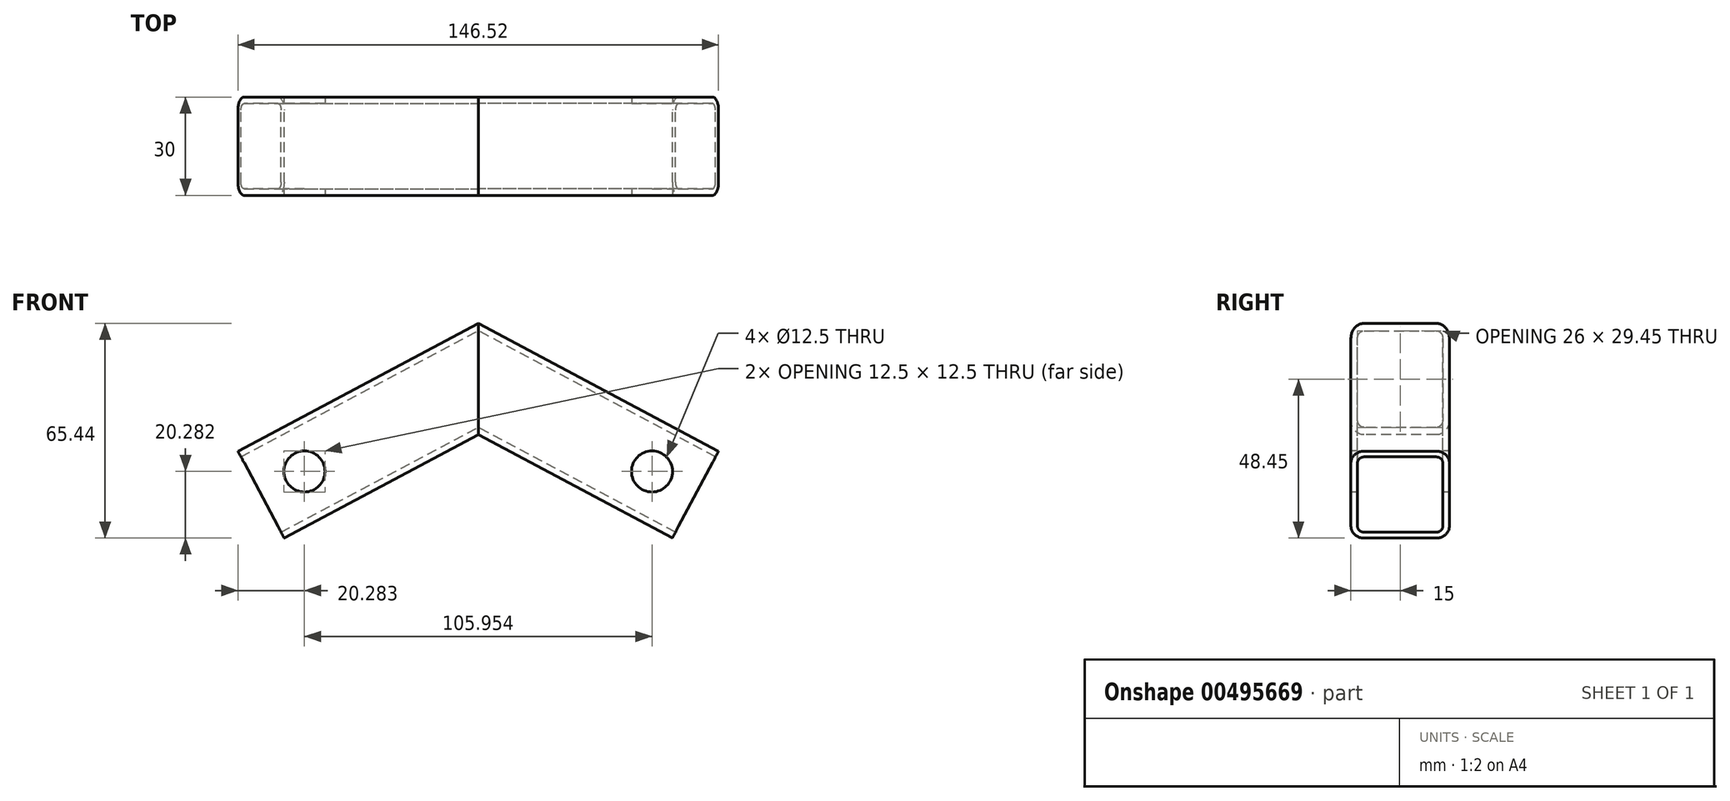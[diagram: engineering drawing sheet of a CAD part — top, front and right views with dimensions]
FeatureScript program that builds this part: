
annotation { "Feature Type Name" : "Feature", "Feature Type Description" : "" }
export const myFeature = defineFeature(function(context is Context, id is Id, definition is map)
    precondition{}
    {
        {
            var Q0;
            Q0=qCreatedBy(makeId("Front.planeOp"),FACE);
            var sketch = newSketch(context, id + "F0", { "sketchPlane" : qUnion([Q0])});
            skLineSegment(sketch, "E0", {"start": v(0, 0) * mm, "end": v(-66.22, -35.21) * mm});
            skSolve(sketch);
        }
        {
            var Q0;
            Q0=sQuery(id+"F0.wireOp",VERTEX,"E0.end");
            var Q1;
            Q1=sQuery(id+"F0.wireOp",EDGE,"E0");
            cPlane(context, id + "F1", {"entities" : qUnion([Q0, Q1]), "cplaneType" : CPlaneType.LINE_POINT, "offset" : 25 * mm, "width" : 150 * mm, "height" : 150 * mm});
        }
        {
            var Q0;
            Q0=qCreatedBy(id+"F1.planeOp",FACE);
            var sketch = newSketch(context, id + "F2", { "sketchPlane" : qUnion([Q0])});
            skLineSegment(sketch, "E1.bottom", {"start": v(11, -15) * mm, "end": v(-11, -15) * mm});
            skLineSegment(sketch, "E1.top", {"start": v(11, 15) * mm, "end": v(-11, 15) * mm});
            skLineSegment(sketch, "E1.left", {"start": v(15, -11) * mm, "end": v(15, 11) * mm});
            skLineSegment(sketch, "E1.right", {"start": v(-15, -11) * mm, "end": v(-15, 11) * mm});
            skPoint(sketch, "E1.middle", {"position": v(0, 0) * mm});
            skPoint(sketch, "E2.visualSharp", {"position": v(-15, 15) * mm});
            skArc(sketch, "E2.filletArc", {"start": v(-11, 15) * mm, "mid": v(-13.83, 13.83) * mm, "end": v(-15, 11) * mm});
            skPoint(sketch, "E3.visualSharp", {"position": v(-15, -15) * mm});
            skArc(sketch, "E3.filletArc", {"start": v(-15, -11) * mm, "mid": v(-13.83, -13.83) * mm, "end": v(-11, -15) * mm});
            skPoint(sketch, "E4.visualSharp", {"position": v(15, -15) * mm});
            skArc(sketch, "E4.filletArc", {"start": v(11, -15) * mm, "mid": v(13.83, -13.83) * mm, "end": v(15, -11) * mm});
            skPoint(sketch, "E5.visualSharp", {"position": v(15, 15) * mm});
            skArc(sketch, "E5.filletArc", {"start": v(15, 11) * mm, "mid": v(13.83, 13.83) * mm, "end": v(11, 15) * mm});
            skArc(sketch, "E6.0", {"start": v(-13, -11) * mm, "mid": v(-12.41, -12.41) * mm, "end": v(-11, -13) * mm});
            skLineSegment(sketch, "E6.1", {"start": v(11, -13) * mm, "end": v(-11, -13) * mm});
            skLineSegment(sketch, "E6.2", {"start": v(-13, -11) * mm, "end": v(-13, 11) * mm});
            skArc(sketch, "E6.3", {"start": v(11, -13) * mm, "mid": v(12.41, -12.41) * mm, "end": v(13, -11) * mm});
            skArc(sketch, "E6.4", {"start": v(-11, 13) * mm, "mid": v(-12.41, 12.41) * mm, "end": v(-13, 11) * mm});
            skLineSegment(sketch, "E6.5", {"start": v(11, 13) * mm, "end": v(-11, 13) * mm});
            skArc(sketch, "E6.6", {"start": v(13, 11) * mm, "mid": v(12.41, 12.41) * mm, "end": v(11, 13) * mm});
            skLineSegment(sketch, "E6.7", {"start": v(13, -11) * mm, "end": v(13, 11) * mm});
            skSolve(sketch);
        }
        {
            var Q0;
            Q0=makeQuery(id+"F2.imprint","IMPRINT",FACE,{"disambiguationData":[TD([[makeQuery(id+"F2.imprint","IMPRINT",EDGE,{"derivedFrom":sQuery(id+"F2.wireOp",EDGE,"E1.bottom")}),-1.0]])]});
            var Q1;
            Q1=sQuery(id+"F0.wireOp",EDGE,"E0");
            sweep(context, id + "F3", {"profiles" : qUnion([Q0]), "path" : qUnion([Q1])});
        }
        {
            var Q0;
            Q0=makeQuery(id+"F3.opSweep","CAP_FACE",FACE,{"disambiguationData":[OSD([sQuery(id+"F0.wireOp",VERTEX,"E0.start"),sQuery(id+"F2.wireOp",EDGE,"E1.bottom"),sQuery(id+"F2.wireOp",EDGE,"E1.top"),sQuery(id+"F2.wireOp",EDGE,"E1.left"),sQuery(id+"F2.wireOp",EDGE,"E1.right"),sQuery(id+"F2.wireOp",EDGE,"E2.filletArc"),sQuery(id+"F2.wireOp",EDGE,"E3.filletArc"),sQuery(id+"F2.wireOp",EDGE,"E4.filletArc"),sQuery(id+"F2.wireOp",EDGE,"E5.filletArc"),sQuery(id+"F2.wireOp",EDGE,"E6.0"),sQuery(id+"F2.wireOp",EDGE,"E6.1"),sQuery(id+"F2.wireOp",EDGE,"E6.2"),sQuery(id+"F2.wireOp",EDGE,"E6.3"),sQuery(id+"F2.wireOp",EDGE,"E6.4"),sQuery(id+"F2.wireOp",EDGE,"E6.5"),sQuery(id+"F2.wireOp",EDGE,"E6.6"),sQuery(id+"F2.wireOp",EDGE,"E6.7")])],"isStart":false});
            extrude(context, id + "F4", {"entities" : qUnion([Q0]), "operationType" : NewBodyOperationType.ADD, "depth" : 25 * mm});
        }
        {
            var Q0;
            {var subQ0=sQuery(id+"F2.wireOp",EDGE,"E1.left");Q0=makeQuery(id+"F4.boolean.opBoolean","MERGE",FACE,{"derivedFrom":[makeQuery(id+"F3.opSweep","SWEPT_FACE",FACE,{"disambiguationData":[OSD([sQuery(id+"F0.wireOp",EDGE,"E0"),subQ0])]}),makeQuery(id+"F4.opExtrude","SWEPT_FACE",FACE,{"disambiguationData":[OSD([sQuery(id+"F0.wireOp",VERTEX,"E0.start"),subQ0])]})]});}
            var sketch = newSketch(context, id + "F5", { "sketchPlane" : qUnion([Q0])});
            skLineSegment(sketch, "E7", {"start": v(0, 16.99) * mm, "end": v(0, -16.99) * mm});
            skLineSegment(sketch, "E8", {"start": v(0, -16.99) * mm, "end": v(29.12, -1.5) * mm});
            skLineSegment(sketch, "E9", {"start": v(29.12, -1.5) * mm, "end": v(15.03, 24.98) * mm});
            skLineSegment(sketch, "E10", {"start": v(15.03, 24.98) * mm, "end": v(0, 16.99) * mm});
            skSolve(sketch);
        }
        {
            var Q0;
            Q0 = qSketchRegion(id + "F5", true);
            extrude(context, id + "F6", {"entities" : qUnion([Q0]), "operationType" : NewBodyOperationType.REMOVE, "endBound" : BoundingType.THROUGH_ALL, "oppositeDirection" : true, "depth" : 25 * mm});
        }
        {
            var Q0;
            {var subQ0=sQuery(id+"F2.wireOp",EDGE,"E1.left");Q0=makeQuery(id+"F4.boolean.opBoolean","MERGE",FACE,{"derivedFrom":[makeQuery(id+"F3.opSweep","SWEPT_FACE",FACE,{"disambiguationData":[OSD([sQuery(id+"F0.wireOp",EDGE,"E0"),subQ0])]}),makeQuery(id+"F4.opExtrude","SWEPT_FACE",FACE,{"disambiguationData":[OSD([sQuery(id+"F0.wireOp",VERTEX,"E0.start"),subQ0])]})]});}
            var sketch = newSketch(context, id + "F7", { "sketchPlane" : qUnion([Q0])});
            skLineSegment(sketch, "E11", {"start": v(-66.22, -35.21) * mm, "end": v(-52.98, -28.17) * mm, "construction": true});
            skCircle(sketch, "E12", {"center": v(-52.98, -28.17) * mm, "radius": 6.25 * mm});
            skSolve(sketch);
        }
        {
            var Q0;
            Q0 = qSketchRegion(id + "F7", true);
            extrude(context, id + "F8", {"entities" : qUnion([Q0]), "operationType" : NewBodyOperationType.REMOVE, "endBound" : BoundingType.THROUGH_ALL, "oppositeDirection" : true, "depth" : 25 * mm});
        }
        {
            var Q0;
            Q0=makeQuery(id+"F3.opSweep","SWEPT_BODY",BODY,{"disambiguationData":[OSD([sQuery(id+"F0.wireOp",EDGE,"E0"),sQuery(id+"F2.wireOp",EDGE,"E1.bottom"),sQuery(id+"F2.wireOp",EDGE,"E1.top"),sQuery(id+"F2.wireOp",EDGE,"E1.left"),sQuery(id+"F2.wireOp",EDGE,"E1.right"),sQuery(id+"F2.wireOp",EDGE,"E2.filletArc"),sQuery(id+"F2.wireOp",EDGE,"E3.filletArc"),sQuery(id+"F2.wireOp",EDGE,"E4.filletArc"),sQuery(id+"F2.wireOp",EDGE,"E5.filletArc"),sQuery(id+"F2.wireOp",EDGE,"E6.0"),sQuery(id+"F2.wireOp",EDGE,"E6.1"),sQuery(id+"F2.wireOp",EDGE,"E6.2"),sQuery(id+"F2.wireOp",EDGE,"E6.3"),sQuery(id+"F2.wireOp",EDGE,"E6.4"),sQuery(id+"F2.wireOp",EDGE,"E6.5"),sQuery(id+"F2.wireOp",EDGE,"E6.6"),sQuery(id+"F2.wireOp",EDGE,"E6.7")])]});
            var Q1;
            Q1=makeQuery(id+"F6.boolean.opBoolean","COPY",FACE,{"derivedFrom":makeQuery(id+"F6.opExtrude","SWEPT_FACE",FACE,{"disambiguationData":[OSD([sQuery(id+"F5.wireOp",EDGE,"E7")])]})});
            mirror(context, id + "F9", {"entities" : qUnion([Q0]), "mirrorPlane" : qUnion([Q1])});
        }
    });
